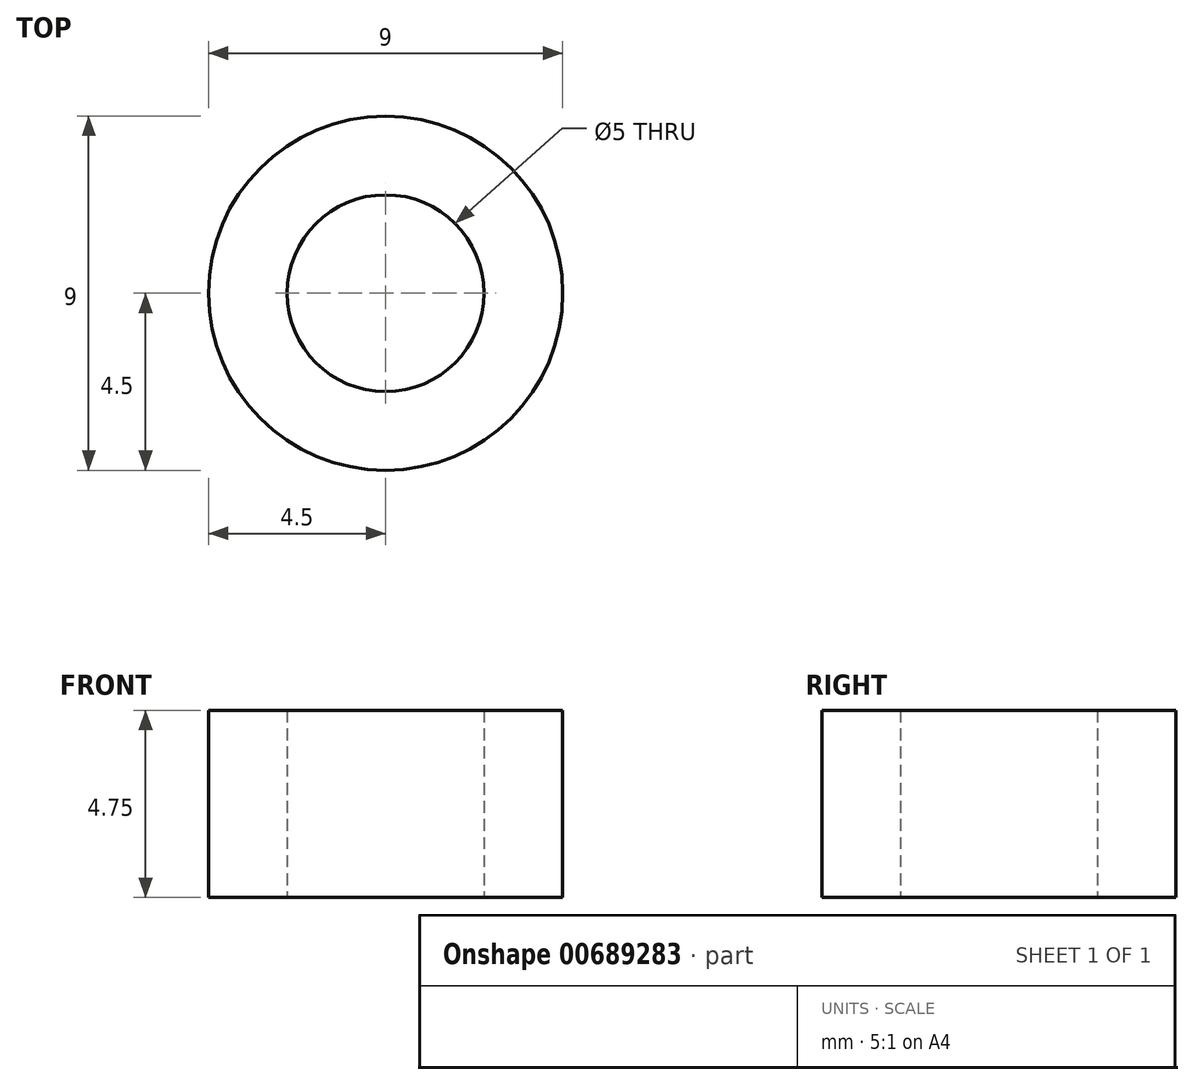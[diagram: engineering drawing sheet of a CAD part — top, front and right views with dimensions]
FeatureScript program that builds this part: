
annotation { "Feature Type Name" : "Feature", "Feature Type Description" : "" }
export const myFeature = defineFeature(function(context is Context, id is Id, definition is map)
    precondition{}
    {
        {
            var Q0;
            Q0=qCreatedBy(makeId("Top.planeOp"),FACE);
            var sketch = newSketch(context, id + "F0", { "sketchPlane" : qUnion([Q0])});
            skCircle(sketch, "E0", {"center": v(0, 0) * mm, "radius": 4.5 * mm});
            skCircle(sketch, "E1", {"center": v(0, 0) * mm, "radius": 2.5 * mm});
            skSolve(sketch);
        }
        {
            var Q0;
            Q0=makeQuery(id+"F0.imprint","IMPRINT",FACE,{"disambiguationData":[TD([[makeQuery(id+"F0.imprint","IMPRINT",EDGE,{"derivedFrom":sQuery(id+"F0.wireOp",EDGE,"E0")}),1.0]])]});
            extrude(context, id + "F1", {"entities" : qUnion([Q0]), "depth" : 4.75 * mm, "offsetDistance" : 25 * mm});
        }
    });
